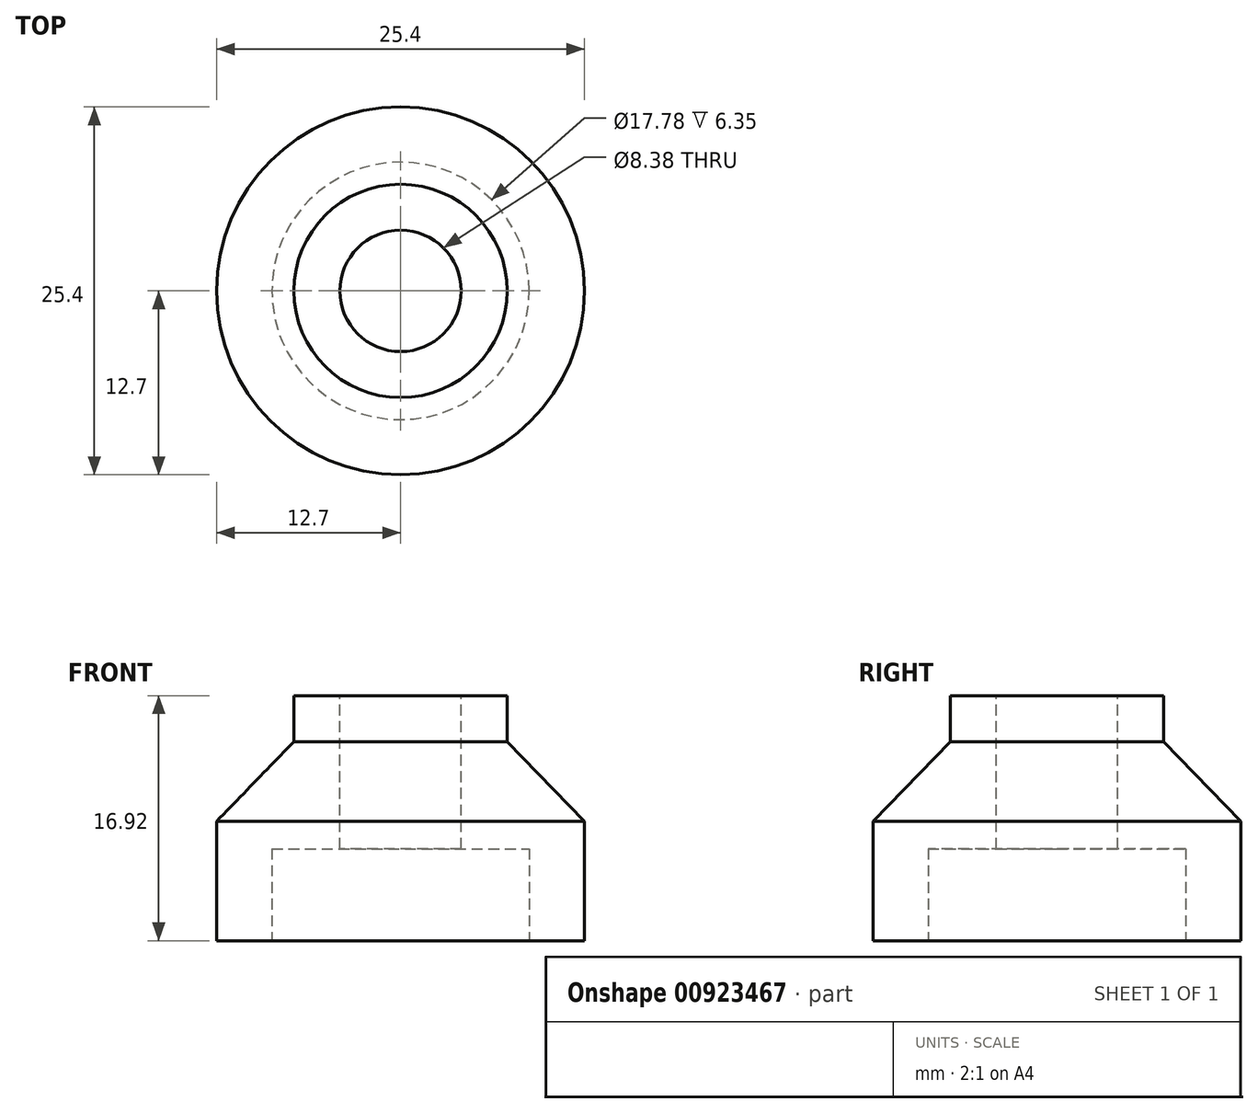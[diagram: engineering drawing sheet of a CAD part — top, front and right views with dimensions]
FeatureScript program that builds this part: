
annotation { "Feature Type Name" : "Feature", "Feature Type Description" : "" }
export const myFeature = defineFeature(function(context is Context, id is Id, definition is map)
    precondition{}
    {
        {
            var Q0;
            Q0=qCreatedBy(makeId("Front.planeOp"),FACE);
            var sketch = newSketch(context, id + "F0", { "sketchPlane" : qUnion([Q0])});
            skLineSegment(sketch, "E0", {"start": v(8.9, 0) * mm, "end": v(8.9, 6.35) * mm});
            skLineSegment(sketch, "E1", {"start": v(8.9, 6.35) * mm, "end": v(0, 6.35) * mm});
            skLineSegment(sketch, "E2", {"start": v(0, 6.35) * mm, "end": v(0, 16.92) * mm});
            skLineSegment(sketch, "E3", {"start": v(0, 16.92) * mm, "end": v(7.37, 16.92) * mm});
            skLineSegment(sketch, "E4", {"start": v(7.37, 16.92) * mm, "end": v(7.37, 13.74) * mm});
            skLineSegment(sketch, "E5", {"start": v(7.37, 13.74) * mm, "end": v(12.7, 8.26) * mm});
            skLineSegment(sketch, "E6", {"start": v(12.7, 8.26) * mm, "end": v(12.7, 0) * mm});
            skLineSegment(sketch, "E7", {"start": v(12.7, 0) * mm, "end": v(8.9, 0) * mm});
            skSolve(sketch);
        }
        {
            var Q0;
            Q0 = qSketchRegion(id + "F0", true);
            var Q1;
            Q1=sQuery(id+"F0.wireOp",EDGE,"E2");
            revolve(context, id + "F1", {"surfaceOperationType" : NewSurfaceOperationType.NEW, "entities" : qUnion([Q0]), "axis" : qUnion([Q1]), "revolveType" : RevolveType.FULL});
        }
        {
            var Q0;
            Q0=makeQuery(id+"F1.opRevolve","SWEPT_FACE",FACE,{"disambiguationData":[OSD([sQuery(id+"F0.wireOp",EDGE,"E3")])]});
            var sketch = newSketch(context, id + "F2", { "sketchPlane" : qUnion([Q0])});
            skCircle(sketch, "E8", {"center": v(0, 0) * mm, "radius": 4.2 * mm});
            skSolve(sketch);
        }
        {
            var Q0;
            Q0 = qSketchRegion(id + "F2", true);
            extrude(context, id + "F3", {"entities" : qUnion([Q0]), "operationType" : NewBodyOperationType.REMOVE, "oppositeDirection" : true, "depth" : 25.4 * mm, "offsetDistance" : 25.4 * mm});
        }
    });
